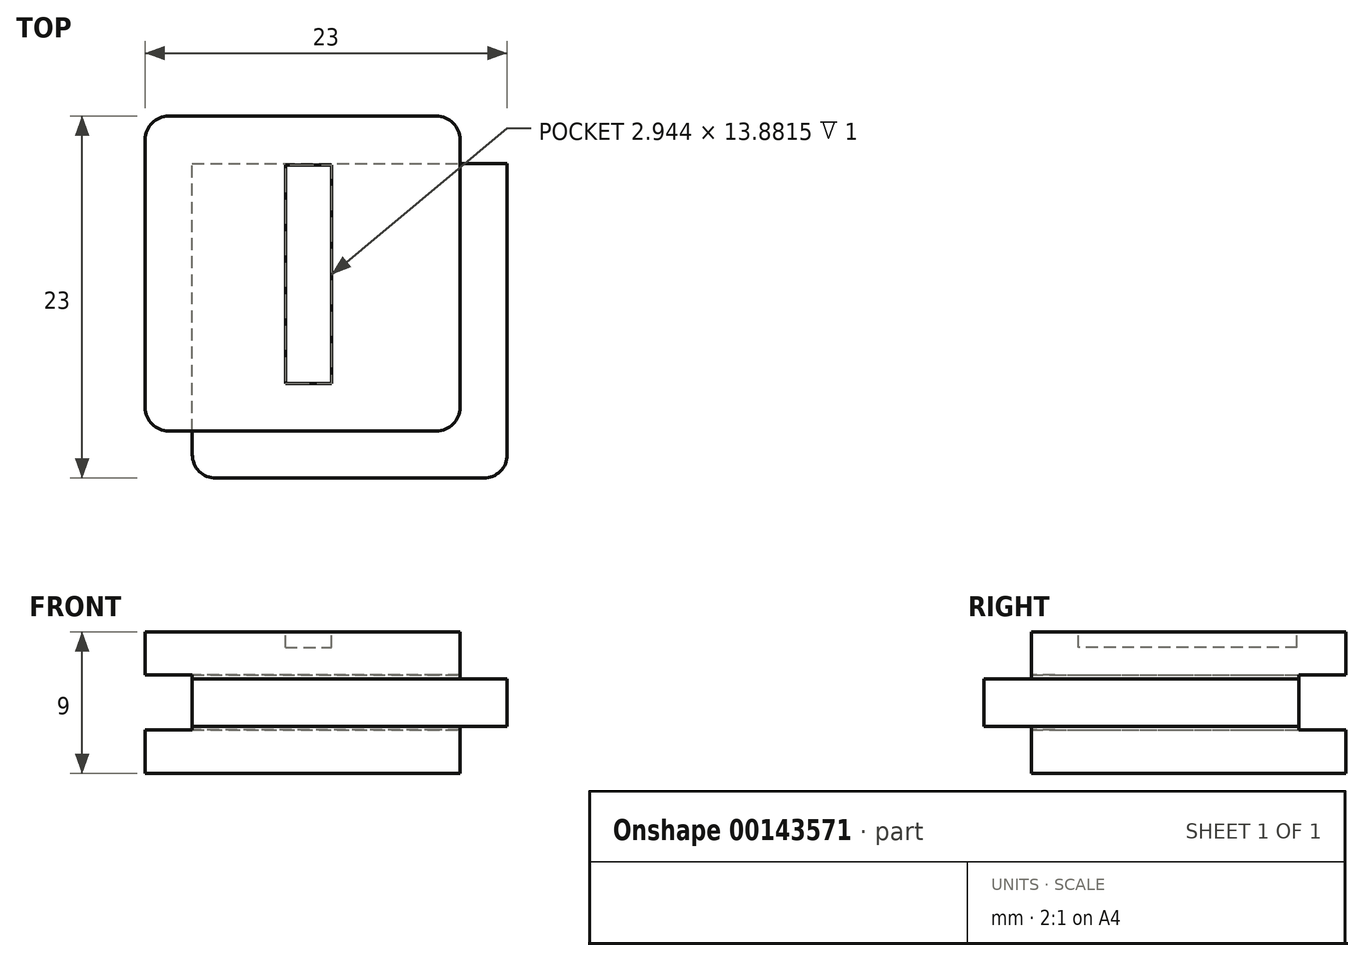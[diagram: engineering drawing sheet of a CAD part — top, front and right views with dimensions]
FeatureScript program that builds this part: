
annotation { "Feature Type Name" : "Feature", "Feature Type Description" : "" }
export const myFeature = defineFeature(function(context is Context, id is Id, definition is map)
    precondition{}
    {
        {
            var Q0;
            Q0=qCreatedBy(makeId("Front.planeOp"),FACE);
            var sketch = newSketch(context, id + "F0", { "sketchPlane" : qUnion([Q0])});
            skLineSegment(sketch, "E0.bottom", {"start": v(10, 4.5) * mm, "end": v(-10, 4.5) * mm});
            skLineSegment(sketch, "E0.top", {"start": v(10, -4.5) * mm, "end": v(-10, -4.5) * mm});
            skLineSegment(sketch, "E0.left", {"start": v(10, 4.5) * mm, "end": v(10, -4.5) * mm});
            skLineSegment(sketch, "E0.right", {"start": v(-10, 4.5) * mm, "end": v(-10, -4.5) * mm});
            skPoint(sketch, "E0.middle", {"position": v(0, 0) * mm});
            skLineSegment(sketch, "E1.bottom", {"start": v(13, 1.5) * mm, "end": v(7, 1.5) * mm});
            skLineSegment(sketch, "E1.top", {"start": v(13, -1.5) * mm, "end": v(7, -1.5) * mm});
            skLineSegment(sketch, "E1.left", {"start": v(13, 1.5) * mm, "end": v(13, -1.5) * mm});
            skLineSegment(sketch, "E1.right", {"start": v(7, 1.5) * mm, "end": v(7, -1.5) * mm});
            skPoint(sketch, "E1.middle", {"position": v(10, 0) * mm});
            skLineSegment(sketch, "E2.bottom", {"start": v(7, 1.5) * mm, "end": v(-7, 1.5) * mm});
            skLineSegment(sketch, "E2.top", {"start": v(7, -1.5) * mm, "end": v(-7, -1.5) * mm});
            skLineSegment(sketch, "E2.right", {"start": v(-7, 1.5) * mm, "end": v(-7, -1.5) * mm});
            skLineSegment(sketch, "E3.bottom", {"start": v(-7, -1.5) * mm, "end": v(-10, -1.5) * mm});
            skLineSegment(sketch, "E3.top", {"start": v(-7, 1.5) * mm, "end": v(-10, 1.5) * mm});
            skLineSegment(sketch, "E3.left", {"start": v(-7, -1.5) * mm, "end": v(-7, 1.5) * mm});
            skLineSegment(sketch, "E3.right", {"start": v(-10, -1.5) * mm, "end": v(-10, 1.5) * mm});
            skSolve(sketch);
        }
        {
            var Q0;
            {var subQ5=sQuery(id+"F0.wireOp",EDGE,"E0.bottom");Q0=makeQuery(id+"F0.imprint","IMPRINT",FACE,{"disambiguationData":[TD([[makeQuery(id+"F0.imprint","IMPRINT",EDGE,{"derivedFrom":subQ5}),1.0]])]});}
            var Q1;
            Q1=makeQuery(id+"F0.imprint","IMPRINT",FACE,{"disambiguationData":[TD([[makeQuery(id+"F0.imprint","IMPRINT",EDGE,{"derivedFrom":sQuery(id+"F0.wireOp",EDGE,"E2.bottom")}),1.0]])]});
            var Q2;
            {var subQ5=sQuery(id+"F0.wireOp",EDGE,"E1.left");Q2=makeQuery(id+"F0.imprint","IMPRINT",FACE,{"disambiguationData":[TD([[makeQuery(id+"F0.imprint","IMPRINT",EDGE,{"derivedFrom":subQ5}),-1.0]])]});}
            var Q3;
            {var subQ5=sQuery(id+"F0.wireOp",EDGE,"E1.right");Q3=makeQuery(id+"F0.imprint","IMPRINT",FACE,{"disambiguationData":[TD([[makeQuery(id+"F0.imprint","IMPRINT",EDGE,{"derivedFrom":subQ5}),1.0]])]});}
            var Q4;
            Q4=makeQuery(id+"F0.imprint","IMPRINT",FACE,{"disambiguationData":[TD([[makeQuery(id+"F0.imprint","IMPRINT",EDGE,{"derivedFrom":sQuery(id+"F0.wireOp",EDGE,"E3.bottom")}),-1.0]])]});
            var Q5;
            {var subQ5=sQuery(id+"F0.wireOp",EDGE,"E0.top");Q5=makeQuery(id+"F0.imprint","IMPRINT",FACE,{"disambiguationData":[TD([[makeQuery(id+"F0.imprint","IMPRINT",EDGE,{"derivedFrom":subQ5}),-1.0]])]});}
            extrude(context, id + "F1", {"entities" : qUnion([Q0, Q1, Q2, Q3, Q4, Q5]), "oppositeDirection" : true, "depth" : 20 * mm});
        }
        {
            var Q0;
            Q0=makeQuery(id+"F0.imprint","IMPRINT",FACE,{"disambiguationData":[TD([[makeQuery(id+"F0.imprint","IMPRINT",EDGE,{"derivedFrom":sQuery(id+"F0.wireOp",EDGE,"E3.bottom")}),-1.0]])]});
            var Q1;
            Q1=makeQuery(id+"F0.imprint","IMPRINT",FACE,{"disambiguationData":[TD([[makeQuery(id+"F0.imprint","IMPRINT",EDGE,{"derivedFrom":sQuery(id+"F0.wireOp",EDGE,"E2.bottom")}),1.0]])]});
            var Q2;
            {var subQ5=sQuery(id+"F0.wireOp",EDGE,"E1.right");Q2=makeQuery(id+"F0.imprint","IMPRINT",FACE,{"disambiguationData":[TD([[makeQuery(id+"F0.imprint","IMPRINT",EDGE,{"derivedFrom":subQ5}),1.0]])]});}
            var Q3;
            {var subQ5=sQuery(id+"F0.wireOp",EDGE,"E1.left");Q3=makeQuery(id+"F0.imprint","IMPRINT",FACE,{"disambiguationData":[TD([[makeQuery(id+"F0.imprint","IMPRINT",EDGE,{"derivedFrom":subQ5}),-1.0]])]});}
            extrude(context, id + "F2", {"entities" : qUnion([Q0, Q1, Q2, Q3]), "operationType" : NewBodyOperationType.ADD, "depth" : 3 * mm});
        }
        {
            var Q0;
            {var subQ0=sQuery(id+"F0.wireOp",EDGE,"E1.left");Q0=makeQuery(id+"F2.boolean.opBoolean","MERGE",FACE,{"derivedFrom":[makeQuery(id+"F1.opExtrude","SWEPT_FACE",FACE,{"disambiguationData":[OSD([subQ0])]}),makeQuery(id+"F2.opExtrude","SWEPT_FACE",FACE,{"disambiguationData":[OSD([subQ0])]})]});}
            var sketch = newSketch(context, id + "F3", { "sketchPlane" : qUnion([Q0])});
            skLineSegment(sketch, "E4.bottom", {"start": v(23, 1.75) * mm, "end": v(17, 1.75) * mm});
            skLineSegment(sketch, "E4.top", {"start": v(23, -1.75) * mm, "end": v(17, -1.75) * mm});
            skLineSegment(sketch, "E4.left", {"start": v(23, 1.75) * mm, "end": v(23, -1.75) * mm});
            skLineSegment(sketch, "E4.right", {"start": v(17, 1.75) * mm, "end": v(17, -1.75) * mm});
            skPoint(sketch, "E4.middle", {"position": v(20, 0) * mm});
            skSolve(sketch);
        }
        {
            var Q0;
            {var subQ1=sQuery(id+"F3.wireOp",EDGE,"E4.bottom");Q0=makeQuery(id+"F3.imprint","IMPRINT",FACE,{"disambiguationData":[TD([[makeQuery(id+"F3.imprint","IMPRINT",EDGE,{"derivedFrom":subQ1}),1.0]])]});}
            var Q1;
            {var subQ1=sQuery(id+"F0.wireOp",EDGE,"E1.left");var subQ8=makeQuery(id+"F1.opExtrude","CAP_EDGE",EDGE,{"disambiguationData":[OSD([subQ1])],"isStart":false});Q1=makeQuery(id+"F3.imprint","IMPRINT",FACE,{"disambiguationData":[TD([[makeQuery(id+"F3.imprint","IMPRINT",EDGE,{"derivedFrom":subQ8}),-1.0]])]});}
            extrude(context, id + "F4", {"entities" : qUnion([Q0, Q1]), "operationType" : NewBodyOperationType.REMOVE, "oppositeDirection" : true, "depth" : 100 * mm});
        }
        {
            var Q0;
            Q0=makeQuery(id+"F4.boolean.opBoolean","COPY",FACE,{"derivedFrom":makeQuery(id+"F4.opExtrude","SWEPT_FACE",FACE,{"disambiguationData":[OSD([sQuery(id+"F3.wireOp",EDGE,"E4.right")])]})});
            var sketch = newSketch(context, id + "F5", { "sketchPlane" : qUnion([Q0])});
            skLineSegment(sketch, "E5.bottom", {"start": v(13, 1.75) * mm, "end": v(7, 1.75) * mm});
            skLineSegment(sketch, "E5.top", {"start": v(13, -1.75) * mm, "end": v(7, -1.75) * mm});
            skLineSegment(sketch, "E5.left", {"start": v(13, 1.75) * mm, "end": v(13, -1.75) * mm});
            skLineSegment(sketch, "E5.right", {"start": v(7, 1.75) * mm, "end": v(7, -1.75) * mm});
            skPoint(sketch, "E5.middle", {"position": v(10, 0) * mm});
            skSolve(sketch);
        }
        {
            var Q0;
            {var subQ3=sQuery(id+"F5.wireOp",EDGE,"E5.left");Q0=makeQuery(id+"F5.imprint","IMPRINT",FACE,{"disambiguationData":[TD([[makeQuery(id+"F5.imprint","IMPRINT",EDGE,{"derivedFrom":subQ3}),-1.0]])]});}
            var Q1;
            {var subQ4=sQuery(id+"F5.wireOp",EDGE,"E5.right");Q1=makeQuery(id+"F5.imprint","IMPRINT",FACE,{"disambiguationData":[TD([[makeQuery(id+"F5.imprint","IMPRINT",EDGE,{"derivedFrom":subQ4}),1.0]])]});}
            extrude(context, id + "F6", {"entities" : qUnion([Q0, Q1]), "operationType" : NewBodyOperationType.REMOVE, "oppositeDirection" : true, "depth" : 100 * mm});
        }
        {
            var Q0;
            Q0=makeQuery(id+"F6.boolean.opBoolean","INTERSECT",EDGE,{"derivedFrom":[makeQuery(id+"F2.opExtrude","CAP_FACE",FACE,{"disambiguationData":[OSD([sQuery(id+"F0.wireOp",EDGE,"E1.bottom"),sQuery(id+"F0.wireOp",EDGE,"E1.top"),sQuery(id+"F0.wireOp",EDGE,"E1.left"),sQuery(id+"F0.wireOp",EDGE,"E2.bottom"),sQuery(id+"F0.wireOp",EDGE,"E2.top"),sQuery(id+"F0.wireOp",EDGE,"E3.bottom"),sQuery(id+"F0.wireOp",EDGE,"E3.top"),sQuery(id+"F0.wireOp",EDGE,"E3.right")])],"isStart":false}),makeQuery(id+"F6.opExtrude","SWEPT_FACE",FACE,{"disambiguationData":[OSD([sQuery(id+"F5.wireOp",EDGE,"E5.right")])]})]});
            var Q1;
            Q1=makeQuery(id+"F2.opExtrude","CAP_EDGE",EDGE,{"disambiguationData":[OSD([sQuery(id+"F0.wireOp",EDGE,"E1.left")])],"isStart":false});
            var Q2;
            {var subQ0=sQuery(id+"F0.wireOp",EDGE,"E0.left");Q2=makeQuery(id+"F1.opExtrude","CAP_EDGE",EDGE,{"disambiguationData":[OSD([subQ0]),TDD([makeQuery(id+"F0.imprint","IMPRINT",EDGE,{"disambiguationData":[TD([[makeQuery(id+"F0.imprint","INTERSECT",VERTEX,{"derivedFrom":[sQuery(id+"F0.wireOp",EDGE,"E0.bottom"),subQ0]}),-1.0]])],"derivedFrom":subQ0})])],"isStart":true});}
            var Q3;
            {var subQ0=sQuery(id+"F0.wireOp",EDGE,"E0.left");Q3=makeQuery(id+"F1.opExtrude","CAP_EDGE",EDGE,{"disambiguationData":[OSD([subQ0]),TDD([makeQuery(id+"F0.imprint","IMPRINT",EDGE,{"disambiguationData":[TD([[makeQuery(id+"F0.imprint","INTERSECT",VERTEX,{"derivedFrom":[sQuery(id+"F0.wireOp",EDGE,"E0.top"),subQ0]}),1.0]])],"derivedFrom":subQ0})])],"isStart":true});}
            var Q4;
            {var subQ0=sQuery(id+"F0.wireOp",EDGE,"E3.right");var subQ1=sQuery(id+"F0.wireOp",EDGE,"E0.right");var subQ3=sQuery(id+"F0.wireOp",EDGE,"E0.top");Q4=makeQuery(id+"F2.boolean.opBoolean","SPLIT",EDGE,{"disambiguationData":[TD([makeQuery(id+"F1.opExtrude","SWEPT_FACE",FACE,{"disambiguationData":[OSD([subQ3])]})])],"derivedFrom":makeQuery(id+"F1.opExtrude","CAP_EDGE",EDGE,{"disambiguationData":[OSD([subQ1,subQ0])],"isStart":true})});}
            var Q5;
            {var subQ1=sQuery(id+"F0.wireOp",EDGE,"E3.right");var subQ2=sQuery(id+"F0.wireOp",EDGE,"E0.right");var subQ3=sQuery(id+"F0.wireOp",EDGE,"E0.bottom");Q5=makeQuery(id+"F2.boolean.opBoolean","SPLIT",EDGE,{"disambiguationData":[TD([makeQuery(id+"F1.opExtrude","SWEPT_FACE",FACE,{"disambiguationData":[OSD([subQ3])]})])],"derivedFrom":makeQuery(id+"F1.opExtrude","CAP_EDGE",EDGE,{"disambiguationData":[OSD([subQ2,subQ1])],"isStart":true})});}
            var Q6;
            Q6=makeQuery(id+"F6.boolean.opBoolean","COPY",EDGE,{"derivedFrom":makeQuery(id+"F6.opExtrude","CAP_EDGE",EDGE,{"disambiguationData":[OSD([sQuery(id+"F5.wireOp",EDGE,"E5.right")])],"isStart":true})});
            var Q7;
            {var subQ0=sQuery(id+"F0.wireOp",EDGE,"E3.right");var subQ1=sQuery(id+"F0.wireOp",EDGE,"E0.right");var subQ2=sQuery(id+"F0.wireOp",EDGE,"E0.bottom");Q7=makeQuery(id+"F4.boolean.opBoolean","SPLIT",EDGE,{"disambiguationData":[TD([makeQuery(id+"F1.opExtrude","SWEPT_FACE",FACE,{"disambiguationData":[OSD([subQ2])]})])],"derivedFrom":makeQuery(id+"F1.opExtrude","CAP_EDGE",EDGE,{"disambiguationData":[OSD([subQ1,subQ0])],"isStart":false})});}
            var Q8;
            {var subQ0=sQuery(id+"F0.wireOp",EDGE,"E3.right");var subQ1=sQuery(id+"F0.wireOp",EDGE,"E0.right");var subQ2=sQuery(id+"F0.wireOp",EDGE,"E0.top");Q8=makeQuery(id+"F4.boolean.opBoolean","SPLIT",EDGE,{"disambiguationData":[TD([makeQuery(id+"F1.opExtrude","SWEPT_FACE",FACE,{"disambiguationData":[OSD([subQ2])]})])],"derivedFrom":makeQuery(id+"F1.opExtrude","CAP_EDGE",EDGE,{"disambiguationData":[OSD([subQ1,subQ0])],"isStart":false})});}
            var Q9;
            Q9=makeQuery(id+"F4.boolean.opBoolean","COPY",EDGE,{"derivedFrom":makeQuery(id+"F4.opExtrude","CAP_EDGE",EDGE,{"disambiguationData":[OSD([sQuery(id+"F3.wireOp",EDGE,"E4.right")])],"isStart":true})});
            var Q10;
            {var subQ0=sQuery(id+"F0.wireOp",EDGE,"E0.left");Q10=makeQuery(id+"F1.opExtrude","CAP_EDGE",EDGE,{"disambiguationData":[OSD([subQ0]),TDD([makeQuery(id+"F0.imprint","IMPRINT",EDGE,{"disambiguationData":[TD([[makeQuery(id+"F0.imprint","INTERSECT",VERTEX,{"derivedFrom":[sQuery(id+"F0.wireOp",EDGE,"E0.bottom"),subQ0]}),-1.0]])],"derivedFrom":subQ0})])],"isStart":false});}
            var Q11;
            {var subQ0=sQuery(id+"F0.wireOp",EDGE,"E0.left");Q11=makeQuery(id+"F1.opExtrude","CAP_EDGE",EDGE,{"disambiguationData":[OSD([subQ0]),TDD([makeQuery(id+"F0.imprint","IMPRINT",EDGE,{"disambiguationData":[TD([[makeQuery(id+"F0.imprint","INTERSECT",VERTEX,{"derivedFrom":[sQuery(id+"F0.wireOp",EDGE,"E0.top"),subQ0]}),1.0]])],"derivedFrom":subQ0})])],"isStart":false});}
            fillet(context, id + "F7", {"entities" : qUnion([Q0, Q1, Q2, Q3, Q4, Q5, Q6, Q7, Q8, Q9, Q10, Q11]), "radius" : 1.5 * mm, "tangentPropagation" : true, "allowEdgeOverflow" : false});
        }
        {
            var Q0;
            Q0=makeQuery(id+"F1.opExtrude","SWEPT_FACE",FACE,{"disambiguationData":[OSD([sQuery(id+"F0.wireOp",EDGE,"E0.bottom")])]});
            var sketch = newSketch(context, id + "F8", { "sketchPlane" : qUnion([Q0])});
            skText(sketch, "E6", { "text": "I", "fontName": "OpenSans-Bold.ttf"});
            skLineSegment(sketch, "E7.0", {"start": v(11.35, 3) * mm, "end": v(-11.07, 3) * mm});
            const initialGuessF8  = {"E6": [-0.00283, 0.003, 1, 0, 0.014]};
            skSetInitialGuess(sketch, initialGuessF8);
            skSolve(sketch);
        }
        {
            var Q0;
            Q0=makeQuery(id+"F8.imprint","IMPRINT",FACE,{"disambiguationData":[TD([[makeQuery(id+"F8.imprint","IMPRINT",EDGE,{"derivedFrom":sQuery(id+"F8.wireOp",EDGE,"E6.sketch_text.stroke-0")}),-1.0]])]});
            extrude(context, id + "F9", {"entities" : qUnion([Q0]), "operationType" : NewBodyOperationType.REMOVE, "oppositeDirection" : true, "depth" : 1 * mm});
        }
    });
